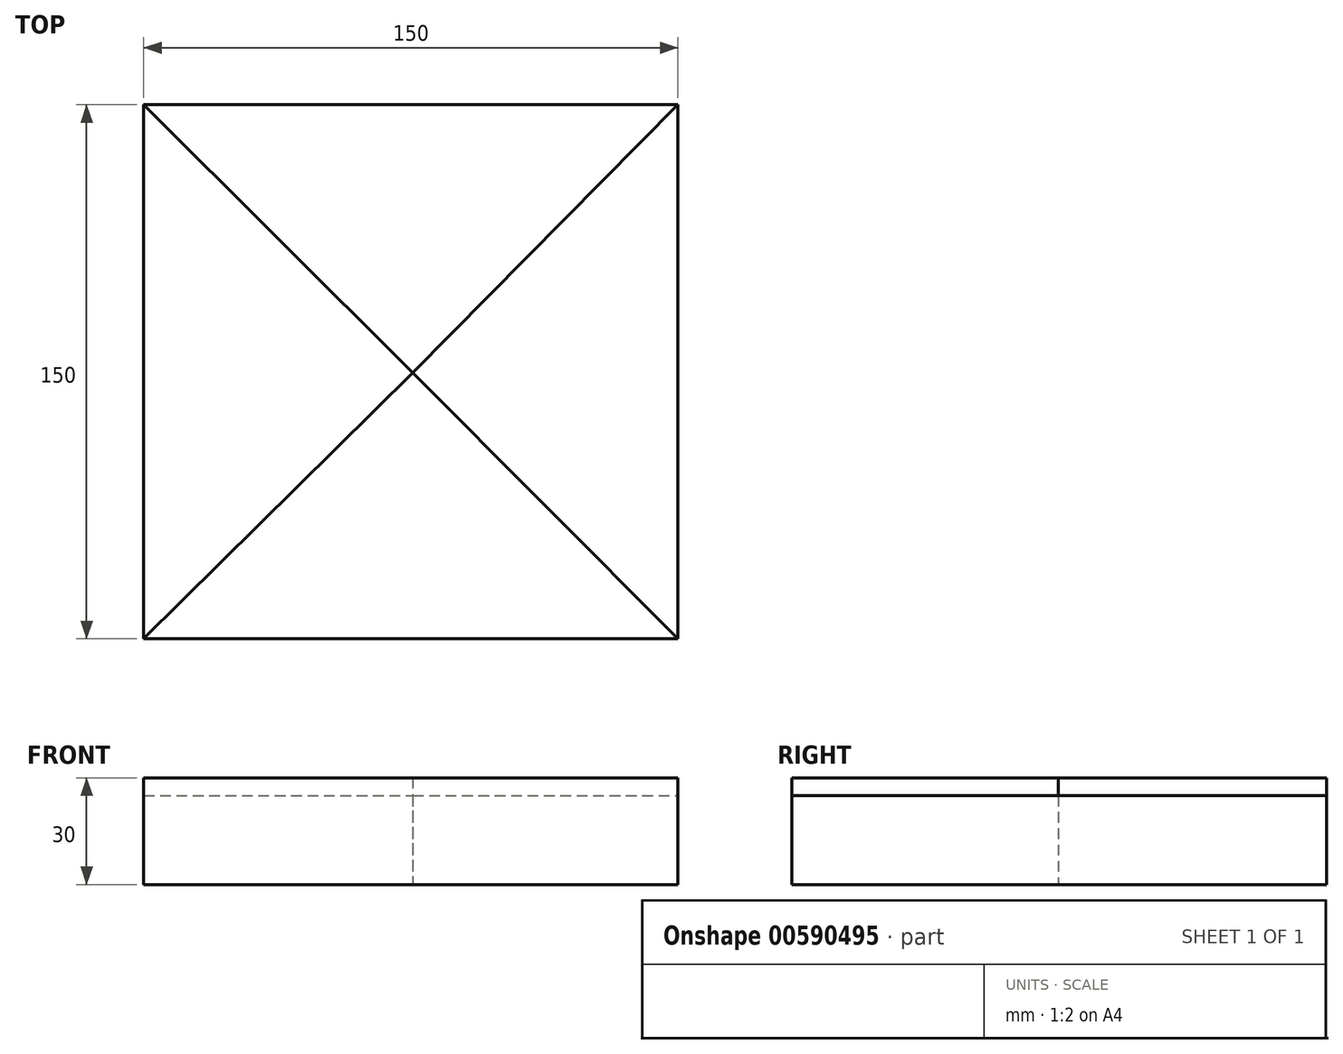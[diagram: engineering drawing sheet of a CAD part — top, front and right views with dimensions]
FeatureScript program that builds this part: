
annotation { "Feature Type Name" : "Feature", "Feature Type Description" : "" }
export const myFeature = defineFeature(function(context is Context, id is Id, definition is map)
    precondition{}
    {
        {
            var Q0;
            Q0=qCreatedBy(makeId("Top.planeOp"),FACE);
            var sketch = newSketch(context, id + "F0", { "sketchPlane" : qUnion([Q0])});
            skLineSegment(sketch, "E0.bottom", {"start": v(-75.56, 75.28) * mm, "end": v(74.44, 75.28) * mm});
            skLineSegment(sketch, "E0.top", {"start": v(-75.56, -74.72) * mm, "end": v(74.44, -74.72) * mm});
            skLineSegment(sketch, "E0.left", {"start": v(-75.56, 75.28) * mm, "end": v(-75.56, -74.72) * mm});
            skLineSegment(sketch, "E0.right", {"start": v(74.44, 75.28) * mm, "end": v(74.44, -74.72) * mm});
            skLineSegment(sketch, "E1", {"start": v(-75.56, 75.28) * mm, "end": v(0, 0) * mm});
            skLineSegment(sketch, "E2", {"start": v(0, 0) * mm, "end": v(-75.56, -74.72) * mm});
            skLineSegment(sketch, "E3", {"start": v(0, 0) * mm, "end": v(74.44, 75.28) * mm});
            skLineSegment(sketch, "E4", {"start": v(0, 0) * mm, "end": v(74.44, -74.72) * mm});
            skSolve(sketch);
        }
        {
            var Q0;
            Q0=makeQuery(id+"F0.imprint","IMPRINT",FACE,{"disambiguationData":[TD([[makeQuery(id+"F0.imprint","IMPRINT",EDGE,{"derivedFrom":sQuery(id+"F0.wireOp",EDGE,"E0.top")}),1.0]])]});
            extrude(context, id + "F1", {"entities" : qUnion([Q0]), "depth" : 30 * mm, "offsetDistance" : 25 * mm});
        }
        {
            var Q0;
            Q0=makeQuery(id+"F0.imprint","IMPRINT",FACE,{"disambiguationData":[TD([[makeQuery(id+"F0.imprint","IMPRINT",EDGE,{"derivedFrom":sQuery(id+"F0.wireOp",EDGE,"E0.bottom")}),-1.0]])]});
            extrude(context, id + "F2", {"entities" : qUnion([Q0]), "depth" : 30 * mm, "offsetDistance" : 25 * mm});
        }
        {
            var Q0;
            Q0=makeQuery(id+"F0.imprint","IMPRINT",FACE,{"disambiguationData":[TD([[makeQuery(id+"F0.imprint","IMPRINT",EDGE,{"derivedFrom":sQuery(id+"F0.wireOp",EDGE,"E0.left")}),1.0]])]});
            extrude(context, id + "F3", {"entities" : qUnion([Q0]), "depth" : 25 * mm, "offsetDistance" : 25 * mm});
        }
        {
            var Q0;
            Q0=makeQuery(id+"F0.imprint","IMPRINT",FACE,{"disambiguationData":[TD([[makeQuery(id+"F0.imprint","IMPRINT",EDGE,{"derivedFrom":sQuery(id+"F0.wireOp",EDGE,"E0.right")}),-1.0]])]});
            extrude(context, id + "F4", {"entities" : qUnion([Q0]), "depth" : 25 * mm, "offsetDistance" : 25 * mm});
        }
    });
